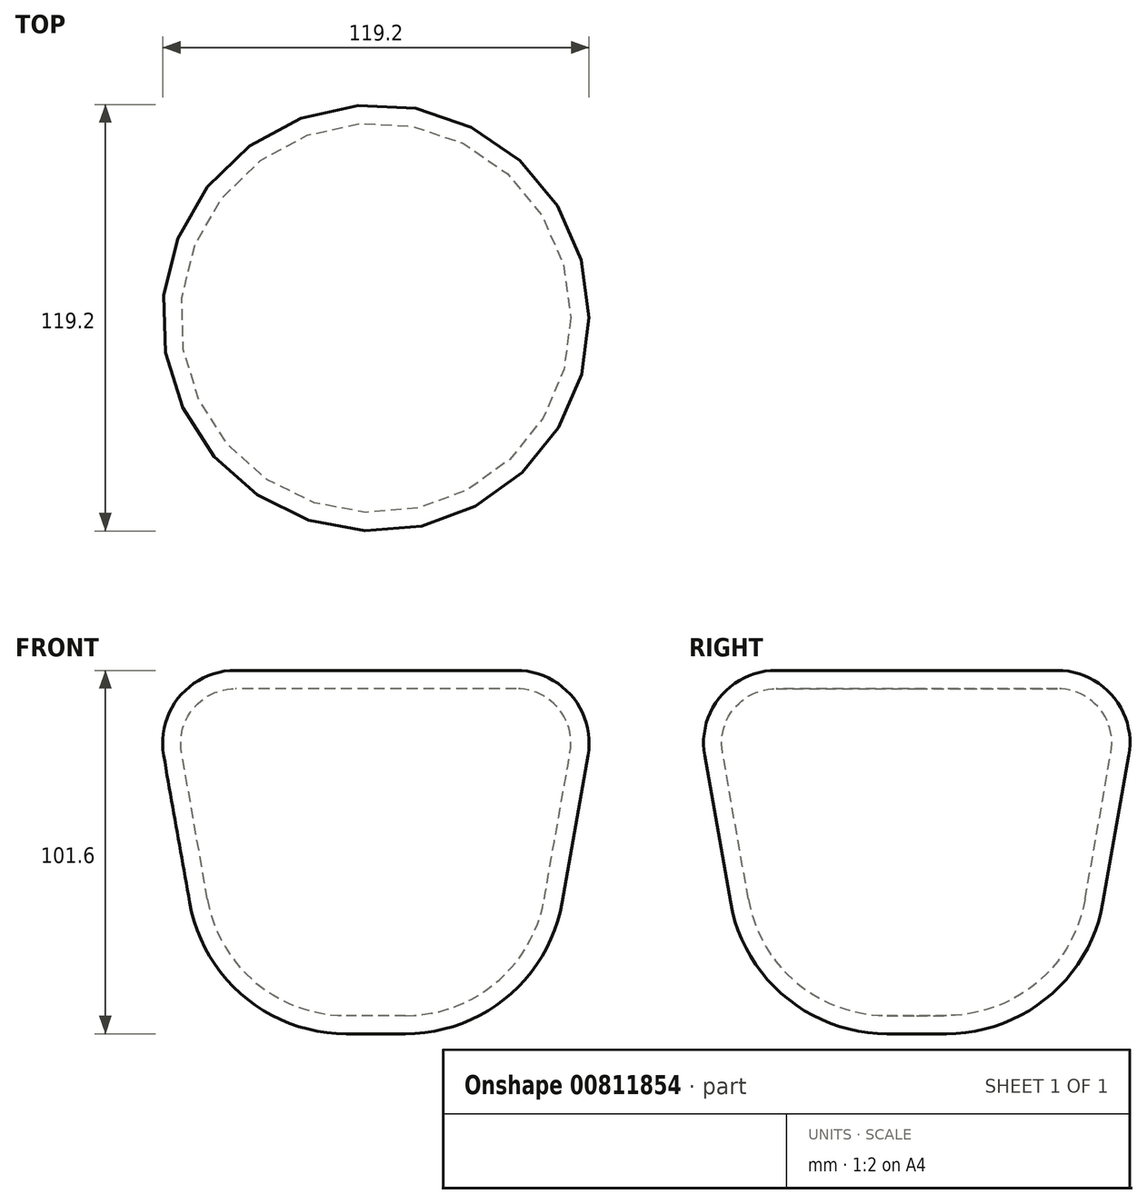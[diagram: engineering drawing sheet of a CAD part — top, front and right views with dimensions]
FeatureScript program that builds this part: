
annotation { "Feature Type Name" : "Feature", "Feature Type Description" : "" }
export const myFeature = defineFeature(function(context is Context, id is Id, definition is map)
    precondition{}
    {
        {
            var Q0;
            Q0=qCreatedBy(makeId("Top.planeOp"),FACE);
            var sketch = newSketch(context, id + "F0", { "sketchPlane" : qUnion([Q0])});
            skCircle(sketch, "E0", {"center": v(0, 0) * mm, "radius": 63.5 * mm});
            skSolve(sketch);
        }
        {
            var Q0;
            Q0=makeQuery(id+"F0.imprint","IMPRINT",FACE,{"disambiguationData":[TD([[makeQuery(id+"F0.imprint","IMPRINT",EDGE,{"derivedFrom":sQuery(id+"F0.wireOp",EDGE,"E0")}),1.0]])]});
            extrude(context, id + "F1", {"entities" : qUnion([Q0]), "oppositeDirection" : true, "depth" : 101.6 * mm, "offsetDistance" : 25.4 * mm, "hasDraft" : true, "draftAngle" : 10 * degree, "draftPullDirection" : true});
        }
        {
            var Q0;
            Q0=makeQuery(id+"F1.opExtrude","CAP_EDGE",EDGE,{"disambiguationData":[OSD([sQuery(id+"F0.wireOp",EDGE,"E0")])],"isStart":false});
            fillet(context, id + "F2", {"entities" : qUnion([Q0]), "radius" : 44.45 * mm, "tangentPropagation" : true, "allowEdgeOverflow" : false});
        }
        {
            var Q0;
            Q0=makeQuery(id+"F1.opExtrude","CAP_EDGE",EDGE,{"disambiguationData":[OSD([sQuery(id+"F0.wireOp",EDGE,"E0")])],"isStart":true});
            fillet(context, id + "F3", {"entities" : qUnion([Q0]), "radius" : 20.32 * mm, "tangentPropagation" : true, "allowEdgeOverflow" : false});
        }
        {
            var Q0;
            Q0=makeQuery(id+"F1.opExtrude","SWEPT_FACE",FACE,{"disambiguationData":[OSD([sQuery(id+"F0.wireOp",EDGE,"E0")])]});
            var Q1;
            Q1=makeQuery(id+"F1.opExtrude","CAP_FACE",FACE,{"disambiguationData":[OSD([sQuery(id+"F0.wireOp",EDGE,"E0")])],"isStart":false});
            var Q2;
            Q2=makeQuery(id+"F3.opFillet","BLEND_FACE",FACE,{"disambiguationData":[OSD([sQuery(id+"F0.wireOp",EDGE,"E0")])]});
            var Q3;
            Q3=makeQuery(id+"F2.opFillet","BLEND_FACE",FACE,{"disambiguationData":[OSD([sQuery(id+"F0.wireOp",EDGE,"E0")])]});
            var Q4;
            Q4=makeQuery(id+"F1.opExtrude","CAP_FACE",FACE,{"disambiguationData":[OSD([sQuery(id+"F0.wireOp",EDGE,"E0")])],"isStart":true});
            var Q5;
            Q5=makeQuery(id+"F1.opExtrude","SWEPT_BODY",BODY,{"disambiguationData":[OSD([sQuery(id+"F0.wireOp",EDGE,"E0")])]});
            shell(context, id + "F4", {"isHollow" : true, "entities" : qUnion([Q0, Q1, Q2, Q3, Q4]), "parts" : qUnion([Q5]), "thickness" : 5.08 * mm});
        }
    });
